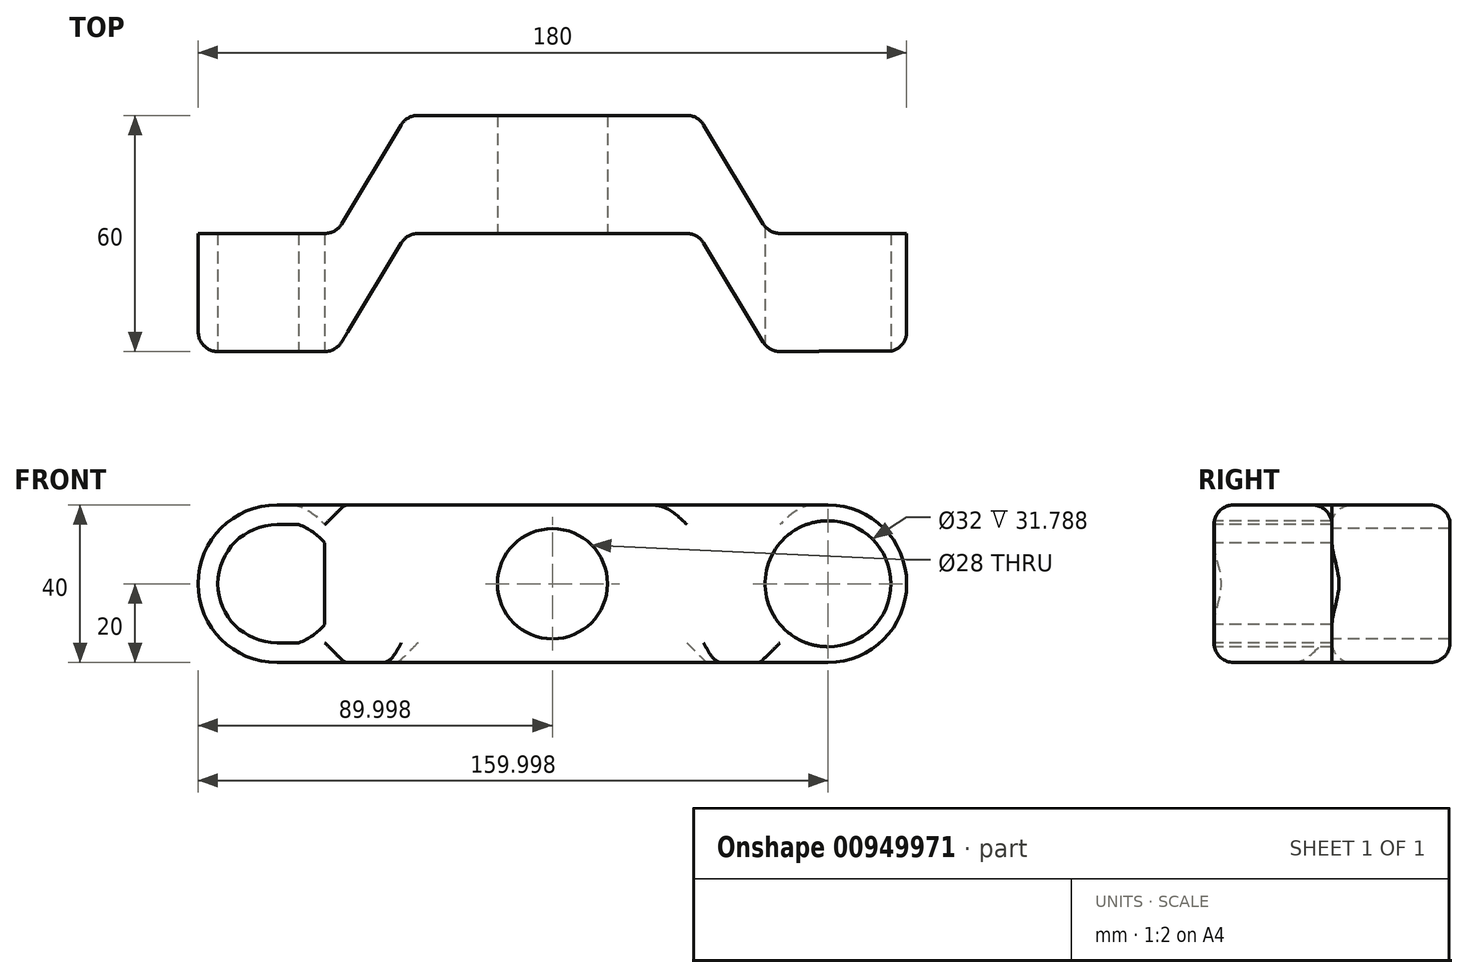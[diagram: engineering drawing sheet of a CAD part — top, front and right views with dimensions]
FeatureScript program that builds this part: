
annotation { "Feature Type Name" : "Feature", "Feature Type Description" : "" }
export const myFeature = defineFeature(function(context is Context, id is Id, definition is map)
    precondition{}
    {
        {
            var Q0;
            Q0=qCreatedBy(makeId("Top.planeOp"),FACE);
            var sketch = newSketch(context, id + "F0", { "sketchPlane" : qUnion([Q0])});
            skLineSegment(sketch, "E0", {"start": v(-72.9, 0) * mm, "end": v(-72.9, 30) * mm});
            skLineSegment(sketch, "E1", {"start": v(-72.9, 30) * mm, "end": v(-37.9, 30) * mm});
            skLineSegment(sketch, "E2", {"start": v(-37.9, 30) * mm, "end": v(-19.87, 60) * mm});
            skLineSegment(sketch, "E3", {"start": v(-19.87, 60) * mm, "end": v(17.1, 60) * mm});
            skLineSegment(sketch, "E4", {"start": v(-72.9, 0) * mm, "end": v(-37.9, 0) * mm});
            skLineSegment(sketch, "E5", {"start": v(-37.9, 0) * mm, "end": v(-19.87, 30) * mm});
            skLineSegment(sketch, "E6", {"start": v(-19.87, 30) * mm, "end": v(17.1, 30) * mm});
            skLineSegment(sketch, "E7", {"start": v(17.1, 86.43) * mm, "end": v(17.1, -10.92) * mm, "construction": true});
            skLineSegment(sketch, "E8.MirrorCS", {"start": v(54.07, 60) * mm, "end": v(17.1, 60) * mm});
            skLineSegment(sketch, "E9.MirrorCS", {"start": v(72.1, 30) * mm, "end": v(54.07, 60) * mm});
            skLineSegment(sketch, "E10.MirrorCS", {"start": v(107.1, 30) * mm, "end": v(72.1, 30) * mm});
            skLineSegment(sketch, "E11.MirrorCS", {"start": v(107.1, 0) * mm, "end": v(107.1, 30) * mm});
            skLineSegment(sketch, "E12.MirrorCS", {"start": v(107.1, 0) * mm, "end": v(72.1, 0) * mm});
            skLineSegment(sketch, "E13.MirrorCS", {"start": v(72.1, 0) * mm, "end": v(54.07, 30) * mm});
            skLineSegment(sketch, "E14.MirrorCS", {"start": v(54.07, 30) * mm, "end": v(17.1, 30) * mm});
            skSolve(sketch);
        }
        {
            var Q0;
            Q0=makeQuery(id+"F0.imprint","IMPRINT",FACE,{"disambiguationData":[TD([[makeQuery(id+"F0.imprint","IMPRINT",EDGE,{"derivedFrom":sQuery(id+"F0.wireOp",EDGE,"E0")}),-1.0]])]});
            extrude(context, id + "F1", {"entities" : qUnion([Q0]), "depth" : 40 * mm, "offsetDistance" : 25 * mm});
        }
        {
            var Q0;
            Q0=makeQuery(id+"F1.opExtrude","CAP_EDGE",EDGE,{"disambiguationData":[OSD([sQuery(id+"F0.wireOp",EDGE,"E0")])],"isStart":false});
            var Q1;
            Q1=makeQuery(id+"F1.opExtrude","CAP_EDGE",EDGE,{"disambiguationData":[OSD([sQuery(id+"F0.wireOp",EDGE,"E0")])],"isStart":true});
            var Q2;
            Q2=makeQuery(id+"F1.opExtrude","CAP_EDGE",EDGE,{"disambiguationData":[OSD([sQuery(id+"F0.wireOp",EDGE,"E11.MirrorCS")])],"isStart":false});
            var Q3;
            Q3=makeQuery(id+"F1.opExtrude","CAP_EDGE",EDGE,{"disambiguationData":[OSD([sQuery(id+"F0.wireOp",EDGE,"E11.MirrorCS")])],"isStart":true});
            fillet(context, id + "F2", {"entities" : qUnion([Q0, Q1, Q2, Q3]), "tangentPropagation" : true, "radius" : 20 * mm, "defaultsChanged" : true, "vertexSettings" : [], "allowEdgeOverflow" : false});
        }
        {
            var Q0;
            Q0=makeQuery(id+"F1.opExtrude","SWEPT_EDGE",EDGE,{"disambiguationData":[OSD([sQuery(id+"F0.wireOp",EDGE,"E4"),sQuery(id+"F0.wireOp",EDGE,"E5")])]});
            var Q1;
            Q1=makeQuery(id+"F1.opExtrude","SWEPT_EDGE",EDGE,{"disambiguationData":[OSD([sQuery(id+"F0.wireOp",EDGE,"E5"),sQuery(id+"F0.wireOp",EDGE,"E6")])]});
            var Q2;
            Q2=makeQuery(id+"F1.opExtrude","SWEPT_EDGE",EDGE,{"disambiguationData":[OSD([sQuery(id+"F0.wireOp",EDGE,"E13.MirrorCS"),sQuery(id+"F0.wireOp",EDGE,"E14.MirrorCS")])]});
            var Q3;
            Q3=makeQuery(id+"F1.opExtrude","SWEPT_EDGE",EDGE,{"disambiguationData":[OSD([sQuery(id+"F0.wireOp",EDGE,"E12.MirrorCS"),sQuery(id+"F0.wireOp",EDGE,"E13.MirrorCS")])]});
            var Q4;
            Q4=makeQuery(id+"F1.opExtrude","SWEPT_EDGE",EDGE,{"disambiguationData":[OSD([sQuery(id+"F0.wireOp",EDGE,"E9.MirrorCS"),sQuery(id+"F0.wireOp",EDGE,"E10.MirrorCS")])]});
            var Q5;
            Q5=makeQuery(id+"F1.opExtrude","SWEPT_EDGE",EDGE,{"disambiguationData":[OSD([sQuery(id+"F0.wireOp",EDGE,"E8.MirrorCS"),sQuery(id+"F0.wireOp",EDGE,"E9.MirrorCS")])]});
            var Q6;
            Q6=makeQuery(id+"F1.opExtrude","SWEPT_EDGE",EDGE,{"disambiguationData":[OSD([sQuery(id+"F0.wireOp",EDGE,"E2"),sQuery(id+"F0.wireOp",EDGE,"E3")])]});
            var Q7;
            Q7=makeQuery(id+"F1.opExtrude","SWEPT_EDGE",EDGE,{"disambiguationData":[OSD([sQuery(id+"F0.wireOp",EDGE,"E1"),sQuery(id+"F0.wireOp",EDGE,"E2")])]});
            var Q8;
            Q8=makeQuery(id+"F1.opExtrude","CAP_EDGE",EDGE,{"disambiguationData":[OSD([sQuery(id+"F0.wireOp",EDGE,"E9.MirrorCS")])],"isStart":false});
            var Q9;
            Q9=makeQuery(id+"F1.opExtrude","CAP_EDGE",EDGE,{"disambiguationData":[OSD([sQuery(id+"F0.wireOp",EDGE,"E3"),sQuery(id+"F0.wireOp",EDGE,"E8.MirrorCS")])],"isStart":false});
            var Q10;
            Q10=makeQuery(id+"F1.opExtrude","CAP_EDGE",EDGE,{"disambiguationData":[OSD([sQuery(id+"F0.wireOp",EDGE,"E2")])],"isStart":false});
            var Q11;
            Q11=makeQuery(id+"F1.opExtrude","CAP_EDGE",EDGE,{"disambiguationData":[OSD([sQuery(id+"F0.wireOp",EDGE,"E13.MirrorCS")])],"isStart":false});
            var Q12;
            Q12=makeQuery(id+"F2.opFillet","BLEND_EDGE",EDGE,{"blendedFrom":[makeQuery(id+"F1.opExtrude","CAP_EDGE",EDGE,{"disambiguationData":[OSD([sQuery(id+"F0.wireOp",EDGE,"E11.MirrorCS")])],"isStart":true}),makeQuery(id+"F1.opExtrude","SWEPT_FACE",FACE,{"disambiguationData":[OSD([sQuery(id+"F0.wireOp",EDGE,"E12.MirrorCS")])]})],"blendedInto":[makeQuery(id+"F1.opExtrude","SWEPT_FACE",FACE,{"disambiguationData":[OSD([sQuery(id+"F0.wireOp",EDGE,"E12.MirrorCS")])]})]});
            var Q13;
            Q13=makeQuery(id+"F2.opFillet","BLEND_EDGE",EDGE,{"blendedFrom":[makeQuery(id+"F1.opExtrude","CAP_EDGE",EDGE,{"disambiguationData":[OSD([sQuery(id+"F0.wireOp",EDGE,"E0")])],"isStart":true}),makeQuery(id+"F1.opExtrude","SWEPT_FACE",FACE,{"disambiguationData":[OSD([sQuery(id+"F0.wireOp",EDGE,"E4")])]})],"blendedInto":[makeQuery(id+"F1.opExtrude","SWEPT_FACE",FACE,{"disambiguationData":[OSD([sQuery(id+"F0.wireOp",EDGE,"E4")])]})]});
            var Q14;
            Q14=makeQuery(id+"F1.opExtrude","CAP_EDGE",EDGE,{"disambiguationData":[OSD([sQuery(id+"F0.wireOp",EDGE,"E6"),sQuery(id+"F0.wireOp",EDGE,"E14.MirrorCS")])],"isStart":true});
            var Q15;
            Q15=makeQuery(id+"F1.opExtrude","CAP_EDGE",EDGE,{"disambiguationData":[OSD([sQuery(id+"F0.wireOp",EDGE,"E3"),sQuery(id+"F0.wireOp",EDGE,"E8.MirrorCS")])],"isStart":true});
            fillet(context, id + "F3", {"entities" : qUnion([Q0, Q1, Q2, Q3, Q4, Q5, Q6, Q7, Q8, Q9, Q10, Q11, Q12, Q13, Q14, Q15]), "tangentPropagation" : true, "radius" : 5 * mm, "defaultsChanged" : false, "vertexSettings" : [], "allowEdgeOverflow" : false});
        }
        {
            var Q0;
            Q0=makeQuery(id+"F1.opExtrude","SWEPT_FACE",FACE,{"disambiguationData":[OSD([sQuery(id+"F0.wireOp",EDGE,"E4")])]});
            var sketch = newSketch(context, id + "F4", { "sketchPlane" : qUnion([Q0])});
            skCircle(sketch, "E15", {"center": v(-52.9, 20) * mm, "radius": 16 * mm});
            skCircle(sketch, "E16", {"center": v(87.1, 20) * mm, "radius": 16 * mm});
            skCircle(sketch, "E17", {"center": v(17.1, 20) * mm, "radius": 14 * mm});
            skSolve(sketch);
        }
        {
            var Q0;
            {var subQ1=sQuery(id+"F0.wireOp",EDGE,"E4");var subQ2=makeQuery(id+"F1.opExtrude","SWEPT_FACE",FACE,{"disambiguationData":[OSD([subQ1])]});var subQ3=subQ2;var subQ9=makeQuery(id+"F3.opFillet","BLEND_EDGE",EDGE,{"blendedFrom":[makeQuery(id+"F2.opFillet","BLEND_EDGE",EDGE,{"blendedFrom":[makeQuery(id+"F1.opExtrude","CAP_EDGE",EDGE,{"disambiguationData":[OSD([sQuery(id+"F0.wireOp",EDGE,"E0")])],"isStart":true}),subQ2],"blendedInto":[subQ2]}),subQ3],"blendedInto":[subQ3]});Q0=makeQuery(id+"F4.imprint","IMPRINT",FACE,{"disambiguationData":[TD([[makeQuery(id+"F4.imprint","IMPRINT",EDGE,{"derivedFrom":subQ9}),1.0]])]});}
            var Q1;
            Q1=makeQuery(id+"F4.imprint","IMPRINT",FACE,{"disambiguationData":[TD([[makeQuery(id+"F4.imprint","IMPRINT",EDGE,{"derivedFrom":sQuery(id+"F4.wireOp",EDGE,"E16")}),1.0]])]});
            var Q2;
            {var subQ0=sQuery(id+"F4.wireOp",EDGE,"E15");var subQ1=sQuery(id+"F0.wireOp",EDGE,"E4");var subQ2=makeQuery(id+"F3.opFillet","BLEND_EDGE",EDGE,{"blendedFrom":[makeQuery(id+"F1.opExtrude","SWEPT_EDGE",EDGE,{"disambiguationData":[OSD([subQ1,sQuery(id+"F0.wireOp",EDGE,"E5")])]}),makeQuery(id+"F1.opExtrude","SWEPT_FACE",FACE,{"disambiguationData":[OSD([subQ1])]})],"blendedInto":[makeQuery(id+"F1.opExtrude","SWEPT_FACE",FACE,{"disambiguationData":[OSD([subQ1])]})]});var subQ3=makeQuery(id+"F4.imprint","INTERSECT",VERTEX,{"disambiguationData":[OD(0.0)],"derivedFrom":[subQ2,subQ0]});Q2=makeQuery(id+"F4.imprint","IMPRINT",FACE,{"disambiguationData":[TD([[makeQuery(id+"F4.imprint","IMPRINT",EDGE,{"disambiguationData":[TD([[subQ3,1.0]])],"derivedFrom":subQ0}),1.0]])]});}
            var Q3;
            Q3=makeQuery(id+"F4.imprint","IMPRINT",FACE,{"disambiguationData":[TD([[makeQuery(id+"F4.imprint","IMPRINT",EDGE,{"derivedFrom":sQuery(id+"F4.wireOp",EDGE,"E17")}),1.0]])]});
            extrude(context, id + "F5", {"entities" : qUnion([Q0, Q1, Q2, Q3]), "operationType" : NewBodyOperationType.REMOVE, "oppositeDirection" : true, "depth" : 66.5 * mm, "offsetDistance" : 25 * mm});
        }
    });
